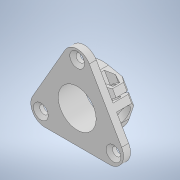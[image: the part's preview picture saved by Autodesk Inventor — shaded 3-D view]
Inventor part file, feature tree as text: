
AUTODESK INVENTOR PART (.ipt)
format: ipt  version: 2022 (Build 260153000, 153)  size: 251,904 bytes
history: native  units: mm
features: extrude x7, sketch x7, projected_geometry x3, hole x2, fillet x1, chamfer x1
ambient origin geometry x8: Origin, YZ Plane, XZ Plane, XY Plane, X Axis, Y Axis, Z Axis, Center Point
bodies: Solid1 (feature_tree)
feature tree (21):
  extrude  "Extrusion1"  Depth=4.0mm
  fillet  "Fillet1"  Radius=4.0mm
  extrude  "Extrusion2"  Depth=16.0mm
  sketch  "Sketch3"  dims[d5=6.0mm d6=3.0mm d7=0.0mm]
  extrude  "Extrusion3"  Depth=3.0mm TaperAngle=0.0deg
  extrude  "Extrusion4"  Depth=6.0mm
  sketch  "Sketch4"  dims[d8=6.0mm d9=3.8mm]
  extrude  "Extrusion5"  Depth=3.0mm
  extrude  "Extrusion6"  Depth=8.0mm TaperAngle=0.0deg
  extrude  "Extrusion7"  Depth=1.5mm
  hole  "Hole1"  [1 undecoded]
  hole  "Hole2"  [1 undecoded]
  chamfer  "Chamfer3"  Distance=6.0mm
  sketch  "Sketch1"  dims[d0=16.2mm d1=4.0mm d2=4.0mm]
  sketch  "Sketch2"  dims[d3=4.0mm d4=16.0mm]
  projected_geometry  "Projected Loop1"
  sketch  "Sketch5"  dims[d10=1.0mm d11=3.0mm]
  sketch  "Sketch6"  dims[d12=3.0mm d13=8.0mm d14=0.0mm]
  projected_geometry  "Projected Loop2"
  sketch  "Sketch7"  dims[d15=3.0mm d16=5.0mm d17=8.75mm d18=0.0mm d19=3.0mm d20=0.0mm d21=6.0mm d22=3.0mm d23=0.0mm d24=0.0mm d25=3.0mm d26=0.0mm d27=0.3mm d28=0.0mm d32=2.0mm d33=2.0mm d34=2.0mm d35=3.6mm d36=6.0mm d37=6.3mm d38=2.0mm d39=90.0deg d40=8.0mm d41=20.594885mm d45=2.9mm d46=6.0mm d47=5.5mm d48=2.0mm d49=90.0deg d50=7.0mm d51=20.594885mm d52=1.5mm d53=2.0mm d54=45.0deg]
  projected_geometry  "Projected Loop3"
note: 2 required parameter values undecoded (feature->parameter linkage not recoverable at this tier; creation-order binding heuristic only, values carry confidence <= 0.55)
